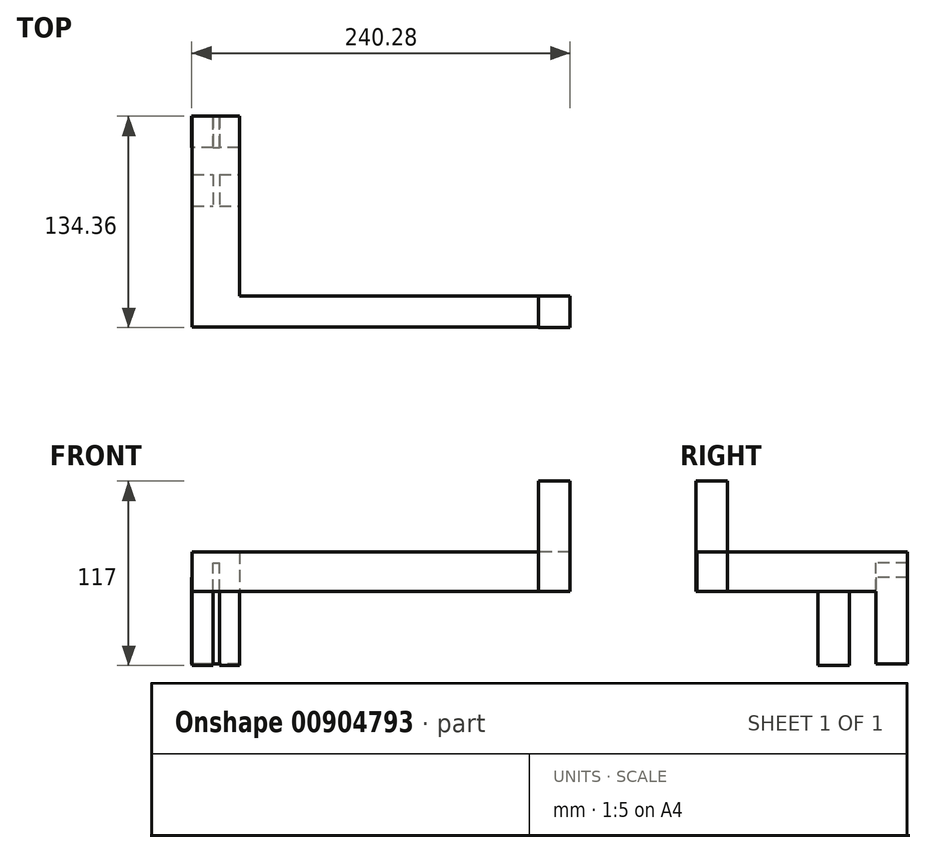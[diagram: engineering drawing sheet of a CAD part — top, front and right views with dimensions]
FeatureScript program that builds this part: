
annotation { "Feature Type Name" : "Feature", "Feature Type Description" : "" }
export const myFeature = defineFeature(function(context is Context, id is Id, definition is map)
    precondition{}
    {
        {
            var Q0;
            Q0=qCreatedBy(makeId("Top.planeOp"),FACE);
            var sketch = newSketch(context, id + "F0", { "sketchPlane" : qUnion([Q0])});
            skLineSegment(sketch, "E0", {"start": v(120.72, -29.97) * mm, "end": v(120.72, -49.47) * mm});
            skLineSegment(sketch, "E1", {"start": v(120.72, -49.47) * mm, "end": v(110.72, -49.47) * mm});
            skLineSegment(sketch, "E2", {"start": v(110.72, -49.62) * mm, "end": v(110.72, -49.47) * mm});
            skLineSegment(sketch, "E3", {"start": v(110.72, -49.62) * mm, "end": v(-119.28, -49.62) * mm});
            skLineSegment(sketch, "E4", {"start": v(-119.28, -49.62) * mm, "end": v(-119.28, 84.31) * mm});
            skLineSegment(sketch, "E5", {"start": v(-119.28, 84.31) * mm, "end": v(-89.28, 84.31) * mm});
            skLineSegment(sketch, "E6", {"start": v(120.72, -29.97) * mm, "end": v(-89.28, -29.97) * mm});
            skLineSegment(sketch, "E7", {"start": v(-89.28, -29.97) * mm, "end": v(-89.28, 84.31) * mm});
            skSolve(sketch);
        }
        {
            var Q0;
            Q0=makeQuery(id+"F0.imprint","IMPRINT",FACE,{"disambiguationData":[TD([[makeQuery(id+"F0.imprint","IMPRINT",EDGE,{"derivedFrom":sQuery(id+"F0.wireOp",EDGE,"E0")}),-1.0]])]});
            extrude(context, id + "F1", {"entities" : qUnion([Q0]), "depth" : 25 * mm, "offsetDistance" : 25 * mm});
        }
        {
            var Q0;
            Q0=makeQuery(id+"F1.opExtrude","SWEPT_FACE",FACE,{"disambiguationData":[OSD([sQuery(id+"F0.wireOp",EDGE,"E5")])]});
            var sketch = newSketch(context, id + "F2", { "sketchPlane" : qUnion([Q0])});
            skLineSegment(sketch, "E8.bottom", {"start": v(89.28, 8.84) * mm, "end": v(119.56, 8.84) * mm});
            skLineSegment(sketch, "E8.top", {"start": v(89.28, -46.16) * mm, "end": v(119.56, -46.16) * mm});
            skLineSegment(sketch, "E8.left", {"start": v(89.28, 8.84) * mm, "end": v(89.28, -46.16) * mm});
            skLineSegment(sketch, "E8.right", {"start": v(119.56, 8.84) * mm, "end": v(119.56, -46.16) * mm});
            skSolve(sketch);
        }
        {
            var Q0;
            {var subQ4=sQuery(id+"F2.wireOp",EDGE,"E8.top");Q0=makeQuery(id+"F2.imprint","IMPRINT",FACE,{"disambiguationData":[TD([[makeQuery(id+"F2.imprint","IMPRINT",EDGE,{"derivedFrom":subQ4}),1.0]])]});}
            var Q1;
            {var subQ2=sQuery(id+"F0.wireOp",EDGE,"E5");var subQ6=makeQuery(id+"F1.opExtrude","CAP_EDGE",EDGE,{"disambiguationData":[OSD([subQ2])],"isStart":true});Q1=makeQuery(id+"F2.imprint","IMPRINT",FACE,{"disambiguationData":[TD([[makeQuery(id+"F2.imprint","IMPRINT",EDGE,{"derivedFrom":subQ6}),-1.0]])]});}
            extrude(context, id + "F3", {"entities" : qUnion([Q0, Q1]), "operationType" : NewBodyOperationType.ADD, "oppositeDirection" : true, "depth" : 20 * mm, "offsetDistance" : 25 * mm});
        }
        {
            var Q0;
            Q0=makeQuery(id+"F1.opExtrude","SWEPT_BODY",BODY,{"disambiguationData":[OSD([sQuery(id+"F0.wireOp",EDGE,"E0"),sQuery(id+"F0.wireOp",EDGE,"E1"),sQuery(id+"F0.wireOp",EDGE,"E2"),sQuery(id+"F0.wireOp",EDGE,"E3"),sQuery(id+"F0.wireOp",EDGE,"E4"),sQuery(id+"F0.wireOp",EDGE,"E5"),sQuery(id+"F0.wireOp",EDGE,"E6"),sQuery(id+"F0.wireOp",EDGE,"E7")])]});
            transform(context, id + "F4", {"entities" : qUnion([Q0]), "transformType" : TransformType.TRANSLATION_3D, "dx" : 104 * mm, "dy" : 0 * mm, "dz" : 0 * mm, "makeCopy" : false});
        }
        {
            var Q0;
            Q0=qCreatedBy(makeId("Top.planeOp"),FACE);
            var sketch = newSketch(context, id + "F5", { "sketchPlane" : qUnion([Q0])});
            skLineSegment(sketch, "E9.bottom", {"start": v(-2, 84.3) * mm, "end": v(2, 84.3) * mm});
            skLineSegment(sketch, "E9.top", {"start": v(-2, 64.3) * mm, "end": v(2, 64.3) * mm});
            skLineSegment(sketch, "E10", {"start": v(2, 84.3) * mm, "end": v(2, 64.3) * mm});
            skLineSegment(sketch, "E11", {"start": v(-2, 84.3) * mm, "end": v(-2, 64.3) * mm});
            skSolve(sketch);
        }
        {
            var Q0;
            Q0=makeQuery(id+"F5.imprint","IMPRINT",FACE,{"disambiguationData":[TD([[makeQuery(id+"F5.imprint","IMPRINT",EDGE,{"derivedFrom":sQuery(id+"F5.wireOp",EDGE,"E9.top")}),1.0]])]});
            extrude(context, id + "F6", {"entities" : qUnion([Q0]), "operationType" : NewBodyOperationType.REMOVE, "endBound" : BoundingType.THROUGH_ALL, "oppositeDirection" : true, "depth" : 25 * mm, "offsetDistance" : 25 * mm, "hasSecondDirection" : true, "secondDirectionOppositeDirection" : false, "secondDirectionDepth" : 18 * mm});
        }
        {
            var Q0;
            Q0=qCreatedBy(makeId("Top.planeOp"),FACE);
            var sketch = newSketch(context, id + "F7", { "sketchPlane" : qUnion([Q0])});
            skLineSegment(sketch, "E12.bottom", {"start": v(204.63, -30.05) * mm, "end": v(224.63, -30.05) * mm});
            skLineSegment(sketch, "E12.top", {"start": v(204.63, -50.05) * mm, "end": v(224.63, -50.05) * mm});
            skLineSegment(sketch, "E12.left", {"start": v(204.63, -30.05) * mm, "end": v(204.63, -50.05) * mm});
            skLineSegment(sketch, "E12.right", {"start": v(224.63, -30.05) * mm, "end": v(224.63, -50.05) * mm});
            skSolve(sketch);
        }
        {
            var Q0;
            Q0=makeQuery(id+"F7.imprint","IMPRINT",FACE,{"disambiguationData":[TD([[makeQuery(id+"F7.imprint","IMPRINT",EDGE,{"derivedFrom":sQuery(id+"F7.wireOp",EDGE,"E12.bottom")}),-1.0]])]});
            extrude(context, id + "F8", {"entities" : qUnion([Q0]), "operationType" : NewBodyOperationType.ADD, "depth" : 70 * mm, "offsetDistance" : 25 * mm});
        }
        {
            var Q0;
            Q0=qCreatedBy(makeId("Top.planeOp"),FACE);
            var sketch = newSketch(context, id + "F9", { "sketchPlane" : qUnion([Q0])});
            skLineSegment(sketch, "E13", {"start": v(-15.36, 47.31) * mm, "end": v(14.77, 47.31) * mm});
            skLineSegment(sketch, "E14", {"start": v(-15.36, 47.31) * mm, "end": v(-15.36, 27.31) * mm});
            skLineSegment(sketch, "E15", {"start": v(14.77, 47.31) * mm, "end": v(14.77, 27.31) * mm});
            skLineSegment(sketch, "E16", {"start": v(-15.36, 27.31) * mm, "end": v(14.77, 27.31) * mm});
            skLineSegment(sketch, "E17.bottom", {"start": v(-2, 47.31) * mm, "end": v(2, 47.31) * mm});
            skLineSegment(sketch, "E17.top", {"start": v(-2, 27.31) * mm, "end": v(2, 27.31) * mm});
            skLineSegment(sketch, "E18", {"start": v(2, 47.31) * mm, "end": v(2, 27.31) * mm});
            skLineSegment(sketch, "E19", {"start": v(-2, 47.31) * mm, "end": v(-2, 27.31) * mm});
            skSolve(sketch);
        }
        {
            var Q0;
            {var subQ2=sQuery(id+"F9.wireOp",EDGE,"E15");var subQ4=sQuery(id+"F9.wireOp",EDGE,"E14");Q0=qUnion([makeQuery(id+"F9.imprint","IMPRINT",FACE,{"disambiguationData":[TD([[makeQuery(id+"F9.imprint","IMPRINT",EDGE,{"derivedFrom":subQ4}),1.0]])]}),makeQuery(id+"F9.imprint","IMPRINT",FACE,{"disambiguationData":[TD([[makeQuery(id+"F9.imprint","IMPRINT",EDGE,{"derivedFrom":subQ2}),-1.0]])]})]);}
            extrude(context, id + "F10", {"entities" : qUnion([Q0]), "operationType" : NewBodyOperationType.ADD, "oppositeDirection" : true, "depth" : 47 * mm, "offsetDistance" : 25 * mm});
        }
    });
